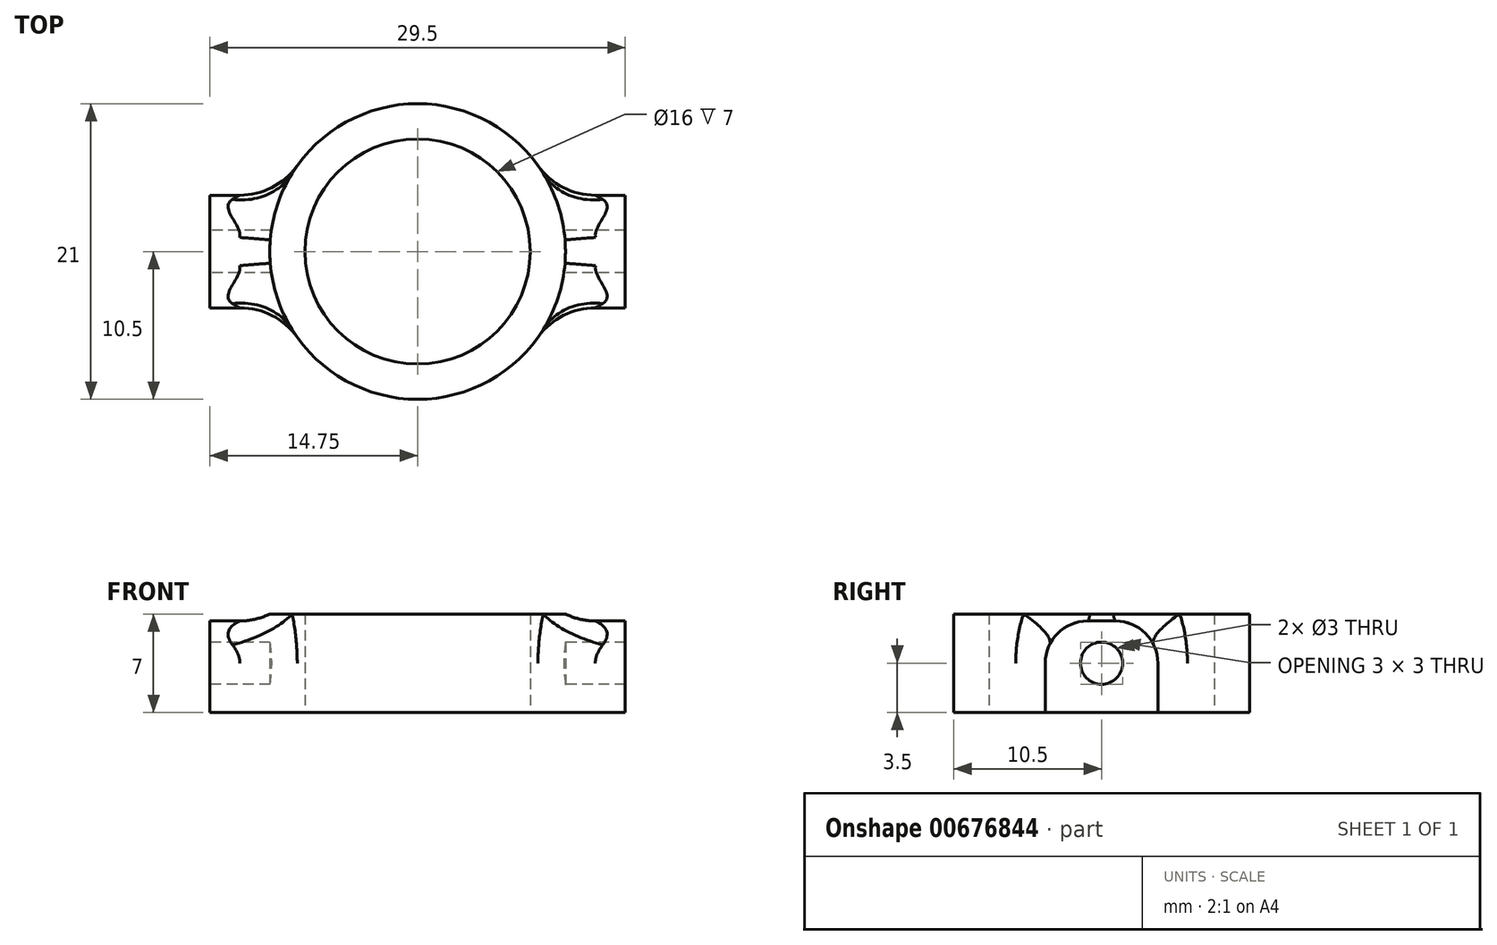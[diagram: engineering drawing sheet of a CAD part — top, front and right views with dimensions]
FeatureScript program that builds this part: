
annotation { "Feature Type Name" : "Feature", "Feature Type Description" : "" }
export const myFeature = defineFeature(function(context is Context, id is Id, definition is map)
    precondition{}
    {
        {
            var Q0;
            Q0=qCreatedBy(makeId("Top.planeOp"),FACE);
            var sketch = newSketch(context, id + "F0", { "sketchPlane" : qUnion([Q0])});
            skCircle(sketch, "E0", {"center": v(0, 0) * mm, "radius": 10.5 * mm});
            skCircle(sketch, "E1", {"center": v(0, 0) * mm, "radius": 8 * mm});
            skSolve(sketch);
        }
        {
            var Q0;
            Q0=makeQuery(id+"F0.imprint","IMPRINT",FACE,{"disambiguationData":[TD([[makeQuery(id+"F0.imprint","IMPRINT",EDGE,{"derivedFrom":sQuery(id+"F0.wireOp",EDGE,"E0")}),1.0]])]});
            extrude(context, id + "F1", {"entities" : qUnion([Q0]), "depth" : 7 * mm, "offsetDistance" : 25 * mm});
        }
        {
            var Q0;
            Q0=qCreatedBy(makeId("Right.planeOp"),FACE);
            var sketch = newSketch(context, id + "F2", { "sketchPlane" : qUnion([Q0])});
            skLineSegment(sketch, "E2.bottom", {"start": v(1, 6.5) * mm, "end": v(-1, 6.5) * mm});
            skLineSegment(sketch, "E2.top", {"start": v(4, 0) * mm, "end": v(-4, 0) * mm});
            skLineSegment(sketch, "E2.left", {"start": v(4, 3.5) * mm, "end": v(4, 0) * mm});
            skLineSegment(sketch, "E2.right", {"start": v(-4, 3.5) * mm, "end": v(-4, 0) * mm});
            skCircle(sketch, "E3", {"center": v(0, 3.5) * mm, "radius": 1.5 * mm});
            skPoint(sketch, "E4.visualSharp", {"position": v(-4, 6.5) * mm});
            skArc(sketch, "E4.filletArc", {"start": v(-1, 6.5) * mm, "mid": v(-3.12, 5.62) * mm, "end": v(-4, 3.5) * mm});
            skPoint(sketch, "E5.visualSharp", {"position": v(4, 6.5) * mm});
            skArc(sketch, "E5.filletArc", {"start": v(4, 3.5) * mm, "mid": v(3.12, 5.62) * mm, "end": v(1, 6.5) * mm});
            skSolve(sketch);
        }
        {
            var Q0;
            Q0=makeQuery(id+"F2.imprint","IMPRINT",FACE,{"disambiguationData":[TD([[makeQuery(id+"F2.imprint","IMPRINT",EDGE,{"derivedFrom":sQuery(id+"F2.wireOp",EDGE,"E2.bottom")}),1.0]])]});
            extrude(context, id + "F3", {"entities" : qUnion([Q0]), "operationType" : NewBodyOperationType.ADD, "endBound" : BoundingType.SYMMETRIC, "depth" : 29.5 * mm, "offsetDistance" : 25 * mm});
        }
        {
            var Q0;
            Q0=makeQuery(id+"F0.imprint","IMPRINT",FACE,{"disambiguationData":[TD([[makeQuery(id+"F0.imprint","IMPRINT",EDGE,{"derivedFrom":sQuery(id+"F0.wireOp",EDGE,"E1")}),1.0]])]});
            extrude(context, id + "F4", {"entities" : qUnion([Q0]), "operationType" : NewBodyOperationType.REMOVE, "endBound" : BoundingType.THROUGH_ALL, "depth" : 25 * mm, "offsetDistance" : 25 * mm});
        }
        {
            var Q0;
            Q0=makeQuery(id+"F3.boolean.opBoolean","INTERSECT",EDGE,{"disambiguationData":[OD(0.0)],"derivedFrom":[makeQuery(id+"F1.opExtrude","SWEPT_FACE",FACE,{"disambiguationData":[OSD([sQuery(id+"F0.wireOp",EDGE,"E0")])]}),makeQuery(id+"F3.opExtrude","SWEPT_FACE",FACE,{"disambiguationData":[OSD([sQuery(id+"F2.wireOp",EDGE,"E4.filletArc")])]})]});
            var Q1;
            Q1=makeQuery(id+"F3.boolean.opBoolean","INTERSECT",EDGE,{"disambiguationData":[OD(1.0)],"derivedFrom":[makeQuery(id+"F1.opExtrude","SWEPT_FACE",FACE,{"disambiguationData":[OSD([sQuery(id+"F0.wireOp",EDGE,"E0")])]}),makeQuery(id+"F3.opExtrude","SWEPT_FACE",FACE,{"disambiguationData":[OSD([sQuery(id+"F2.wireOp",EDGE,"E4.filletArc")])]})]});
            fillet(context, id + "F5", {"entities" : qUnion([Q0, Q1]), "radius" : 5 * mm, "tangentPropagation" : true, "allowEdgeOverflow" : false});
        }
    });
